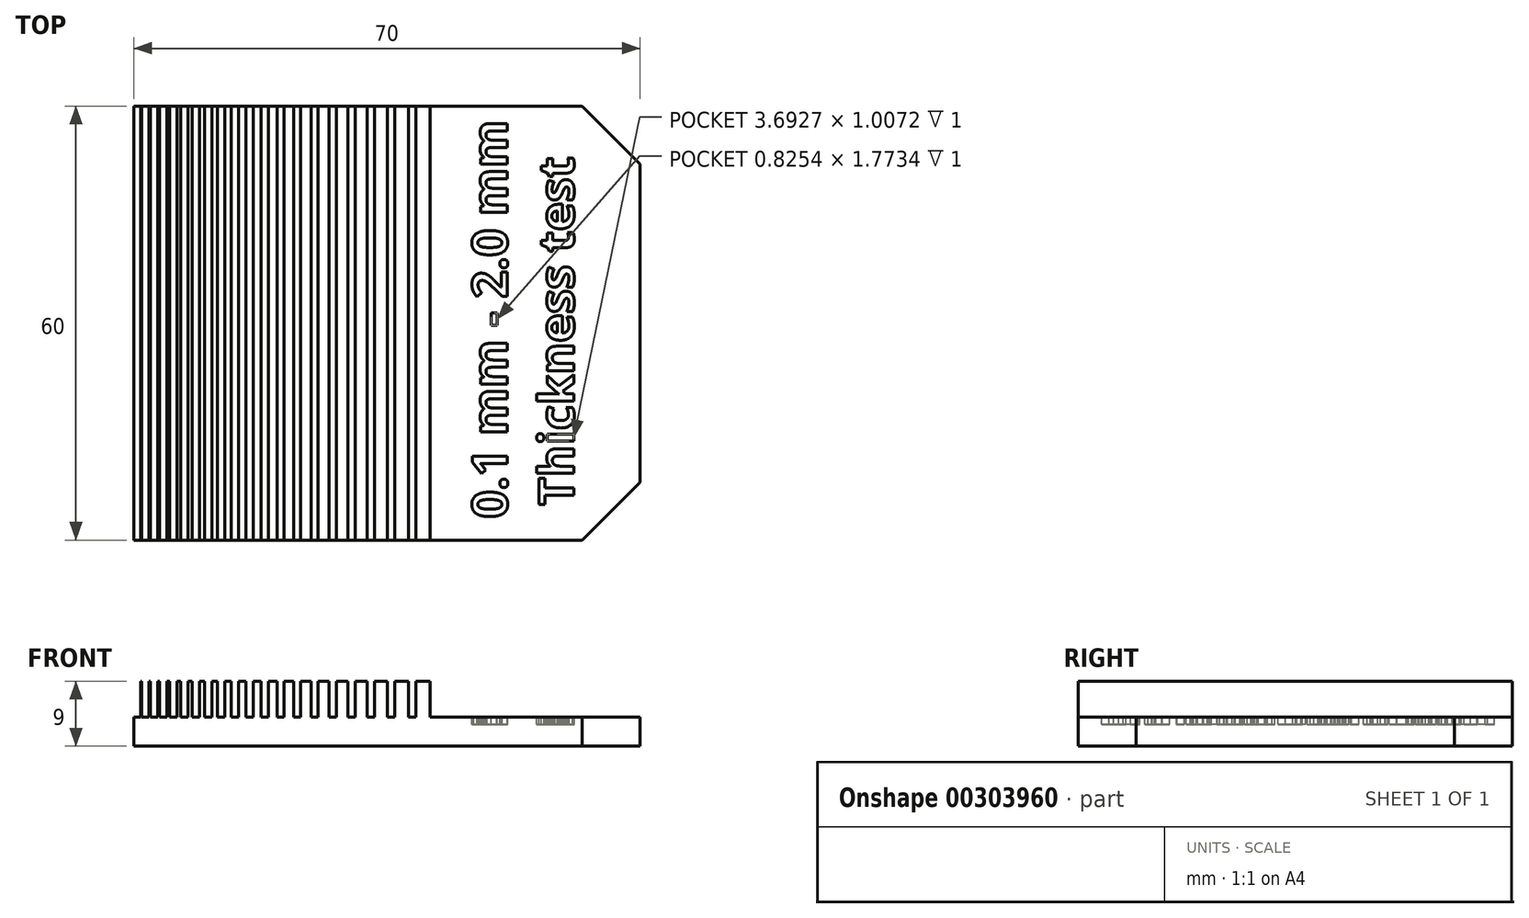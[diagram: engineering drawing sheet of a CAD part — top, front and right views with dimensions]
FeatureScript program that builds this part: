
annotation { "Feature Type Name" : "Feature", "Feature Type Description" : "" }
export const myFeature = defineFeature(function(context is Context, id is Id, definition is map)
    precondition{}
    {
        {
            var Q0;
            Q0=qCreatedBy(makeId("Top.planeOp"),FACE);
            var sketch = newSketch(context, id + "F0", { "sketchPlane" : qUnion([Q0])});
            skLineSegment(sketch, "E0.bottom", {"start": v(-35, -30) * mm, "end": v(35, -30) * mm});
            skLineSegment(sketch, "E0.top", {"start": v(-35, 30) * mm, "end": v(35, 30) * mm});
            skLineSegment(sketch, "E0.left", {"start": v(-35, -30) * mm, "end": v(-35, 30) * mm});
            skLineSegment(sketch, "E0.right", {"start": v(35, -30) * mm, "end": v(35, 30) * mm});
            skSolve(sketch);
        }
        {
            var Q0;
            Q0=makeQuery(id+"F0.imprint","IMPRINT",FACE,{"disambiguationData":[TD([[makeQuery(id+"F0.imprint","IMPRINT",EDGE,{"derivedFrom":sQuery(id+"F0.wireOp",EDGE,"E0.bottom")}),1.0]])]});
            extrude(context, id + "F1", {"entities" : qUnion([Q0]), "depth" : 4 * mm});
        }
        {
            var Q0;
            Q0=makeQuery(id+"F1.opExtrude","CAP_FACE",FACE,{"disambiguationData":[OSD([sQuery(id+"F0.wireOp",EDGE,"E0.bottom"),sQuery(id+"F0.wireOp",EDGE,"E0.top"),sQuery(id+"F0.wireOp",EDGE,"E0.left"),sQuery(id+"F0.wireOp",EDGE,"E0.right")])],"isStart":false});
            var sketch = newSketch(context, id + "F2", { "sketchPlane" : qUnion([Q0])});
            skLineSegment(sketch, "E1.bottom", {"start": v(-34, -30) * mm, "end": v(-33.9, -30) * mm});
            skLineSegment(sketch, "E1.top", {"start": v(-34, 30) * mm, "end": v(-33.9, 30) * mm});
            skLineSegment(sketch, "E1.left", {"start": v(-34, -30) * mm, "end": v(-34, 30) * mm});
            skLineSegment(sketch, "E1.right", {"start": v(-33.9, -30) * mm, "end": v(-33.9, 30) * mm});
            skLineSegment(sketch, "E2.bottom", {"start": v(-32.9, -30) * mm, "end": v(-32.7, -30) * mm});
            skLineSegment(sketch, "E2.top", {"start": v(-32.9, 30) * mm, "end": v(-32.7, 30) * mm});
            skLineSegment(sketch, "E2.left", {"start": v(-32.9, -30) * mm, "end": v(-32.9, 30) * mm});
            skLineSegment(sketch, "E2.right", {"start": v(-32.7, -30) * mm, "end": v(-32.7, 30) * mm});
            skLineSegment(sketch, "E3.bottom", {"start": v(-31.7, -30) * mm, "end": v(-31.4, -30) * mm});
            skLineSegment(sketch, "E3.top", {"start": v(-31.7, 30) * mm, "end": v(-31.4, 30) * mm});
            skLineSegment(sketch, "E3.left", {"start": v(-31.7, -30) * mm, "end": v(-31.7, 30) * mm});
            skLineSegment(sketch, "E3.right", {"start": v(-31.4, -30) * mm, "end": v(-31.4, 30) * mm});
            skLineSegment(sketch, "E4.bottom", {"start": v(-30.4, -30) * mm, "end": v(-30, -30) * mm});
            skLineSegment(sketch, "E4.top", {"start": v(-30.4, 30) * mm, "end": v(-30, 30) * mm});
            skLineSegment(sketch, "E4.left", {"start": v(-30.4, -30) * mm, "end": v(-30.4, 30) * mm});
            skLineSegment(sketch, "E4.right", {"start": v(-30, -30) * mm, "end": v(-30, 30) * mm});
            skLineSegment(sketch, "E5.bottom", {"start": v(-29, -30) * mm, "end": v(-28.5, -30) * mm});
            skLineSegment(sketch, "E5.top", {"start": v(-29, 30) * mm, "end": v(-28.5, 30) * mm});
            skLineSegment(sketch, "E5.left", {"start": v(-29, -30) * mm, "end": v(-29, 30) * mm});
            skLineSegment(sketch, "E5.right", {"start": v(-28.5, -30) * mm, "end": v(-28.5, 30) * mm});
            skLineSegment(sketch, "E6.bottom", {"start": v(-27.5, -30) * mm, "end": v(-26.9, -30) * mm});
            skLineSegment(sketch, "E6.top", {"start": v(-27.5, 30) * mm, "end": v(-26.9, 30) * mm});
            skLineSegment(sketch, "E6.left", {"start": v(-27.5, -30) * mm, "end": v(-27.5, 30) * mm});
            skLineSegment(sketch, "E6.right", {"start": v(-26.9, -30) * mm, "end": v(-26.9, 30) * mm});
            skLineSegment(sketch, "E7.bottom", {"start": v(-25.9, -30) * mm, "end": v(-25.2, -30) * mm});
            skLineSegment(sketch, "E7.top", {"start": v(-25.9, 30) * mm, "end": v(-25.2, 30) * mm});
            skLineSegment(sketch, "E7.left", {"start": v(-25.9, -30) * mm, "end": v(-25.9, 30) * mm});
            skLineSegment(sketch, "E7.right", {"start": v(-25.2, -30) * mm, "end": v(-25.2, 30) * mm});
            skLineSegment(sketch, "E8.bottom", {"start": v(-24.2, -30) * mm, "end": v(-23.4, -30) * mm});
            skLineSegment(sketch, "E8.top", {"start": v(-24.2, 30) * mm, "end": v(-23.4, 30) * mm});
            skLineSegment(sketch, "E8.left", {"start": v(-24.2, -30) * mm, "end": v(-24.2, 30) * mm});
            skLineSegment(sketch, "E8.right", {"start": v(-23.4, -30) * mm, "end": v(-23.4, 30) * mm});
            skLineSegment(sketch, "E9.bottom", {"start": v(-22.4, -30) * mm, "end": v(-21.5, -30) * mm});
            skLineSegment(sketch, "E9.top", {"start": v(-22.4, 30) * mm, "end": v(-21.5, 30) * mm});
            skLineSegment(sketch, "E9.left", {"start": v(-22.4, -30) * mm, "end": v(-22.4, 30) * mm});
            skLineSegment(sketch, "E9.right", {"start": v(-21.5, -30) * mm, "end": v(-21.5, 30) * mm});
            skLineSegment(sketch, "E10.bottom", {"start": v(-20.5, -30) * mm, "end": v(-19.5, -30) * mm});
            skLineSegment(sketch, "E10.top", {"start": v(-20.5, 30) * mm, "end": v(-19.5, 30) * mm});
            skLineSegment(sketch, "E10.left", {"start": v(-20.5, -30) * mm, "end": v(-20.5, 30) * mm});
            skLineSegment(sketch, "E10.right", {"start": v(-19.5, -30) * mm, "end": v(-19.5, 30) * mm});
            skLineSegment(sketch, "E11.bottom", {"start": v(-18.5, -30) * mm, "end": v(-17.4, -30) * mm});
            skLineSegment(sketch, "E11.top", {"start": v(-18.5, 30) * mm, "end": v(-17.4, 30) * mm});
            skLineSegment(sketch, "E11.left", {"start": v(-18.5, -30) * mm, "end": v(-18.5, 30) * mm});
            skLineSegment(sketch, "E11.right", {"start": v(-17.4, -30) * mm, "end": v(-17.4, 30) * mm});
            skLineSegment(sketch, "E12.bottom", {"start": v(-16.4, -30) * mm, "end": v(-15.2, -30) * mm});
            skLineSegment(sketch, "E12.top", {"start": v(-16.4, 30) * mm, "end": v(-15.2, 30) * mm});
            skLineSegment(sketch, "E12.left", {"start": v(-16.4, -30) * mm, "end": v(-16.4, 30) * mm});
            skLineSegment(sketch, "E12.right", {"start": v(-15.2, -30) * mm, "end": v(-15.2, 30) * mm});
            skLineSegment(sketch, "E13.bottom", {"start": v(-14.2, -30) * mm, "end": v(-12.9, -30) * mm});
            skLineSegment(sketch, "E13.top", {"start": v(-14.2, 30) * mm, "end": v(-12.9, 30) * mm});
            skLineSegment(sketch, "E13.left", {"start": v(-14.2, -30) * mm, "end": v(-14.2, 30) * mm});
            skLineSegment(sketch, "E13.right", {"start": v(-12.9, -30) * mm, "end": v(-12.9, 30) * mm});
            skLineSegment(sketch, "E14.bottom", {"start": v(-11.9, -30) * mm, "end": v(-10.5, -30) * mm});
            skLineSegment(sketch, "E14.top", {"start": v(-11.9, 30) * mm, "end": v(-10.5, 30) * mm});
            skLineSegment(sketch, "E14.left", {"start": v(-11.9, -30) * mm, "end": v(-11.9, 30) * mm});
            skLineSegment(sketch, "E14.right", {"start": v(-10.5, -30) * mm, "end": v(-10.5, 30) * mm});
            skLineSegment(sketch, "E15.bottom", {"start": v(-9.5, -30) * mm, "end": v(-8, -30) * mm});
            skLineSegment(sketch, "E15.top", {"start": v(-9.5, 30) * mm, "end": v(-8, 30) * mm});
            skLineSegment(sketch, "E15.left", {"start": v(-9.5, -30) * mm, "end": v(-9.5, 30) * mm});
            skLineSegment(sketch, "E15.right", {"start": v(-8, -30) * mm, "end": v(-8, 30) * mm});
            skLineSegment(sketch, "E16.bottom", {"start": v(-7, -30) * mm, "end": v(-5.4, -30) * mm});
            skLineSegment(sketch, "E16.top", {"start": v(-7, 30) * mm, "end": v(-5.4, 30) * mm});
            skLineSegment(sketch, "E16.left", {"start": v(-7, -30) * mm, "end": v(-7, 30) * mm});
            skLineSegment(sketch, "E16.right", {"start": v(-5.4, -30) * mm, "end": v(-5.4, 30) * mm});
            skLineSegment(sketch, "E17.bottom", {"start": v(-4.4, -30) * mm, "end": v(-2.7, -30) * mm});
            skLineSegment(sketch, "E17.top", {"start": v(-4.4, 30) * mm, "end": v(-2.7, 30) * mm});
            skLineSegment(sketch, "E17.left", {"start": v(-4.4, -30) * mm, "end": v(-4.4, 30) * mm});
            skLineSegment(sketch, "E17.right", {"start": v(-2.7, -30) * mm, "end": v(-2.7, 30) * mm});
            skLineSegment(sketch, "E18.bottom", {"start": v(1.1, -30) * mm, "end": v(3, -30) * mm});
            skLineSegment(sketch, "E18.top", {"start": v(1.1, 30) * mm, "end": v(3, 30) * mm});
            skLineSegment(sketch, "E18.left", {"start": v(1.1, -30) * mm, "end": v(1.1, 30) * mm});
            skLineSegment(sketch, "E18.right", {"start": v(3, -30) * mm, "end": v(3, 30) * mm});
            skLineSegment(sketch, "E19.bottom", {"start": v(4, -30) * mm, "end": v(6, -30) * mm});
            skLineSegment(sketch, "E19.top", {"start": v(4, 30) * mm, "end": v(6, 30) * mm});
            skLineSegment(sketch, "E19.left", {"start": v(4, -30) * mm, "end": v(4, 30) * mm});
            skLineSegment(sketch, "E19.right", {"start": v(6, -30) * mm, "end": v(6, 30) * mm});
            skLineSegment(sketch, "E20.bottom", {"start": v(0.1, -30) * mm, "end": v(-1.7, -30) * mm});
            skLineSegment(sketch, "E20.top", {"start": v(0.1, 30) * mm, "end": v(-1.7, 30) * mm});
            skLineSegment(sketch, "E20.left", {"start": v(0.1, -30) * mm, "end": v(0.1, 30) * mm});
            skLineSegment(sketch, "E20.right", {"start": v(-1.7, -30) * mm, "end": v(-1.7, 30) * mm});
            skSolve(sketch);
        }
        {
            var Q0;
            Q0 = qSketchRegion(id + "F2", true);
            extrude(context, id + "F3", {"entities" : qUnion([Q0]), "operationType" : NewBodyOperationType.ADD, "depth" : 5 * mm});
        }
        {
            var Q0;
            {var subQ0=sQuery(id+"F0.wireOp",EDGE,"E0.top");var subQ1=sQuery(id+"F0.wireOp",EDGE,"E0.right");var subQ2=sQuery(id+"F0.wireOp",EDGE,"E0.bottom");Q0=makeQuery(id+"F3.boolean.opBoolean","SPLIT",FACE,{"disambiguationData":[TD([makeQuery(id+"F1.opExtrude","SWEPT_FACE",FACE,{"disambiguationData":[OSD([subQ1])]})])],"derivedFrom":makeQuery(id+"F1.opExtrude","CAP_FACE",FACE,{"disambiguationData":[OSD([subQ2,subQ0,sQuery(id+"F0.wireOp",EDGE,"E0.left"),subQ1])],"isStart":false})});}
            var sketch = newSketch(context, id + "F4", { "sketchPlane" : qUnion([Q0])});
            skText(sketch, "E21", { "text": "0.1 mm - 2.0 mm\n Thickness test", "fontName": "OpenSans-Bold.ttf"});
            const initialGuessF4  = {"E21": [0.01665, -0.02699, 0, 1, 0.00487]};
            skSetInitialGuess(sketch, initialGuessF4);
            skSolve(sketch);
        }
        {
            var Q0;
            Q0 = qSketchRegion(id + "F4", true);
            extrude(context, id + "F5", {"entities" : qUnion([Q0]), "operationType" : NewBodyOperationType.REMOVE, "oppositeDirection" : true, "depth" : 1 * mm});
        }
        {
            var Q0;
            Q0=makeQuery(id+"F1.opExtrude","SWEPT_EDGE",EDGE,{"disambiguationData":[OSD([sQuery(id+"F0.wireOp",EDGE,"E0.bottom"),sQuery(id+"F0.wireOp",EDGE,"E0.right")])]});
            var Q1;
            Q1=makeQuery(id+"F1.opExtrude","SWEPT_EDGE",EDGE,{"disambiguationData":[OSD([sQuery(id+"F0.wireOp",EDGE,"E0.top"),sQuery(id+"F0.wireOp",EDGE,"E0.right")])]});
            chamfer(context, id + "F6", {"entities" : qUnion([Q0, Q1]), "width" : 8 * mm, "tangentPropagation" : true});
        }
    });
